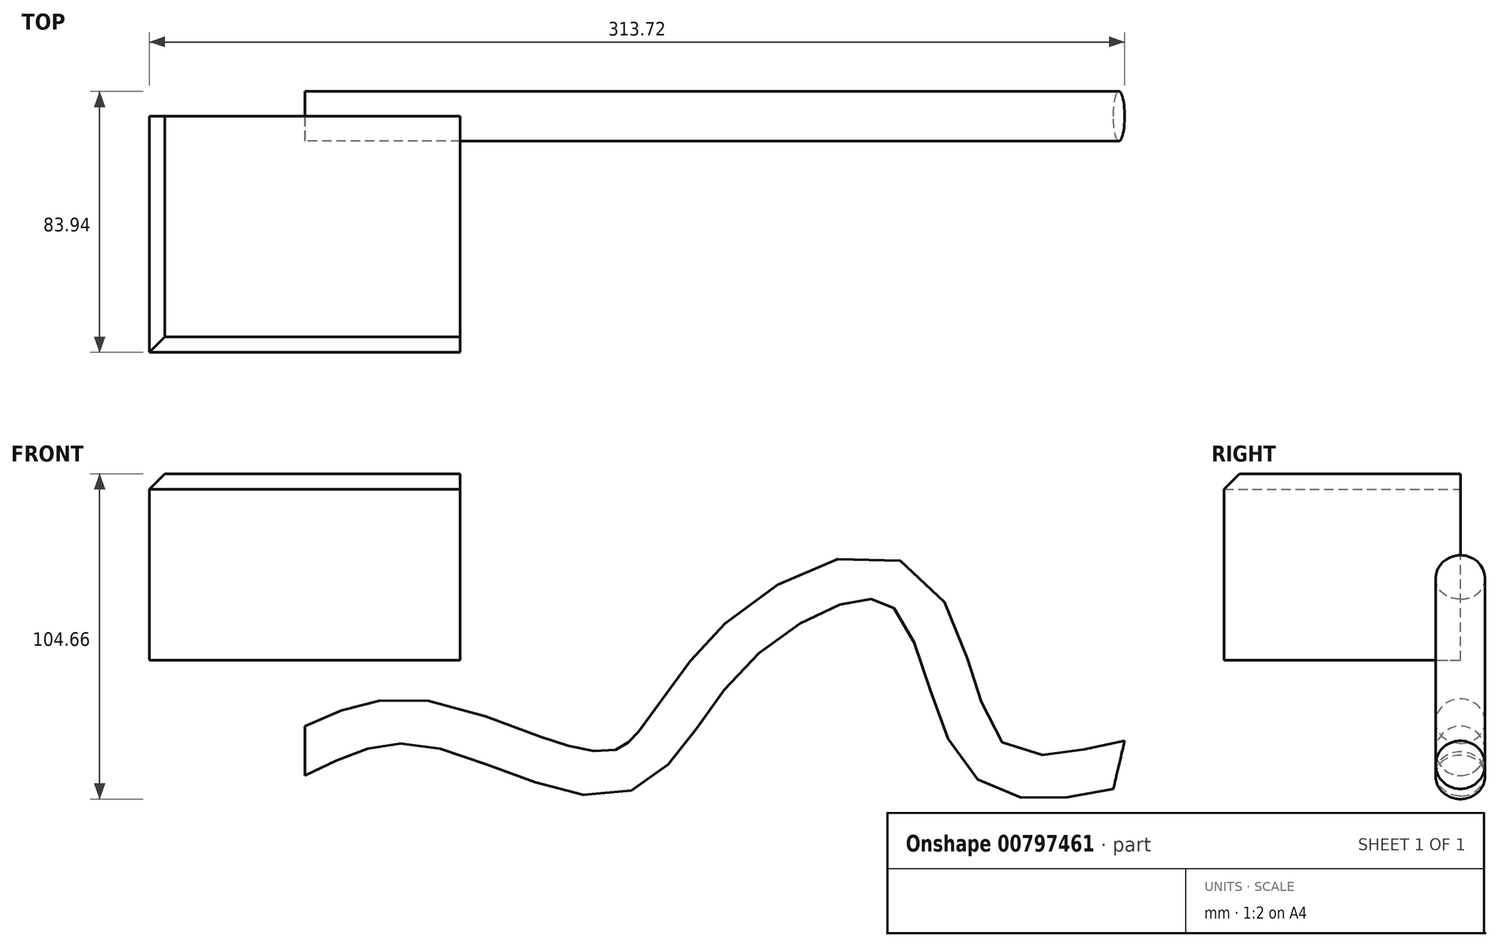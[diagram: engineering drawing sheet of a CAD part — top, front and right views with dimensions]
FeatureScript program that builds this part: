
annotation { "Feature Type Name" : "Feature", "Feature Type Description" : "" }
export const myFeature = defineFeature(function(context is Context, id is Id, definition is map)
    precondition{}
    {
        {
            var Q0;
            Q0=qCreatedBy(makeId("Front.planeOp"),FACE);
            var sketch = newSketch(context, id + "F0", { "sketchPlane" : qUnion([Q0])});
            skLineSegment(sketch, "E0.bottom", {"start": v(50, -30) * mm, "end": v(-50, -30) * mm});
            skLineSegment(sketch, "E0.top", {"start": v(50, 30) * mm, "end": v(-50, 30) * mm});
            skLineSegment(sketch, "E0.left", {"start": v(50, -30) * mm, "end": v(50, 30) * mm});
            skLineSegment(sketch, "E0.right", {"start": v(-50, -30) * mm, "end": v(-50, 30) * mm});
            skPoint(sketch, "E0.middle", {"position": v(0, 0) * mm});
            skLineSegment(sketch, "E1.bottom", {"start": v(63.87, 47.54) * mm, "end": v(114.08, 47.54) * mm});
            skLineSegment(sketch, "E1.top", {"start": v(63.87, 105.86) * mm, "end": v(114.08, 105.86) * mm});
            skLineSegment(sketch, "E1.left", {"start": v(63.87, 47.54) * mm, "end": v(63.87, 105.86) * mm});
            skLineSegment(sketch, "E1.right", {"start": v(114.08, 47.54) * mm, "end": v(114.08, 105.86) * mm});
            skPoint(sketch, "E1.middle", {"position": v(88.98, 76.7) * mm});
            skLineSegment(sketch, "E2", {"start": v(50, 30) * mm, "end": v(50, 65.09) * mm});
            skArc(sketch, "E3", {"start": v(50, 65.09) * mm, "mid": v(55.25, 78.66) * mm, "end": v(68.26, 85.18) * mm});
            skArc(sketch, "E4.0", {"start": v(40, 65.09) * mm, "mid": v(47.84, 85.39) * mm, "end": v(67.3, 95.14) * mm});
            skLineSegment(sketch, "E4.1", {"start": v(40, 34.66) * mm, "end": v(40, 65.09) * mm});
            skSolve(sketch);
        }
        {
            var Q0;
            Q0=makeQuery(id+"F0.imprint","IMPRINT",FACE,{"disambiguationData":[TD([[makeQuery(id+"F0.imprint","IMPRINT",EDGE,{"derivedFrom":sQuery(id+"F0.wireOp",EDGE,"E0.bottom")}),-1.0]])]});
            extrude(context, id + "F1", {"entities" : qUnion([Q0]), "depth" : 76 * mm, "offsetDistance" : 25 * mm});
        }
        {
            var Q0;
            Q0=qCreatedBy(makeId("Right.planeOp"),FACE);
            var sketch = newSketch(context, id + "F2", { "sketchPlane" : qUnion([Q0])});
            skCircle(sketch, "E5", {"center": v(0, -59.18) * mm, "radius": 7.94 * mm});
            skSolve(sketch);
        }
        {
            var Q0;
            Q0=qCreatedBy(makeId("Front.planeOp"),FACE);
            var sketch = newSketch(context, id + "F3", { "sketchPlane" : qUnion([Q0])});
            skFitSpline(sketch, "E6", {"points": [v(0, -59.26) * mm, v(39.4, -50.42) * mm, v(99.62, -65.95) * mm, v(135.43, -28.23) * mm, v(192.17, -6.68) * mm, v(218.79, -60.56) * mm, v(261.9, -63.73) * mm], "startDerivative": vector(244.45, 116.67) * mm, "endDerivative": vector(332.92, 73.13) * mm});
            skSolve(sketch);
        }
        {
            var Q0;
            Q0=makeQuery(id+"F2.imprint","IMPRINT",FACE,{"disambiguationData":[TD([[makeQuery(id+"F2.imprint","IMPRINT",EDGE,{"derivedFrom":sQuery(id+"F2.wireOp",EDGE,"E5")}),1.0]])]});
            var Q1;
            Q1=sQuery(id+"F3.wireOp",EDGE,"E6");
            sweep(context, id + "F4", {"profiles" : qUnion([Q0]), "path" : qUnion([Q1])});
        }
        {
            var Q0;
            Q0=makeQuery(id+"F1.opExtrude","CAP_EDGE",EDGE,{"disambiguationData":[OSD([sQuery(id+"F0.wireOp",EDGE,"E0.top")])],"isStart":false});
            var Q1;
            Q1=makeQuery(id+"F1.opExtrude","SWEPT_EDGE",EDGE,{"disambiguationData":[OSD([sQuery(id+"F0.wireOp",EDGE,"E0.top"),sQuery(id+"F0.wireOp",EDGE,"E0.right")])]});
            chamfer(context, id + "F5", {"entities" : qUnion([Q0, Q1]), "width" : 5 * mm, "tangentPropagation" : true});
        }
    });
